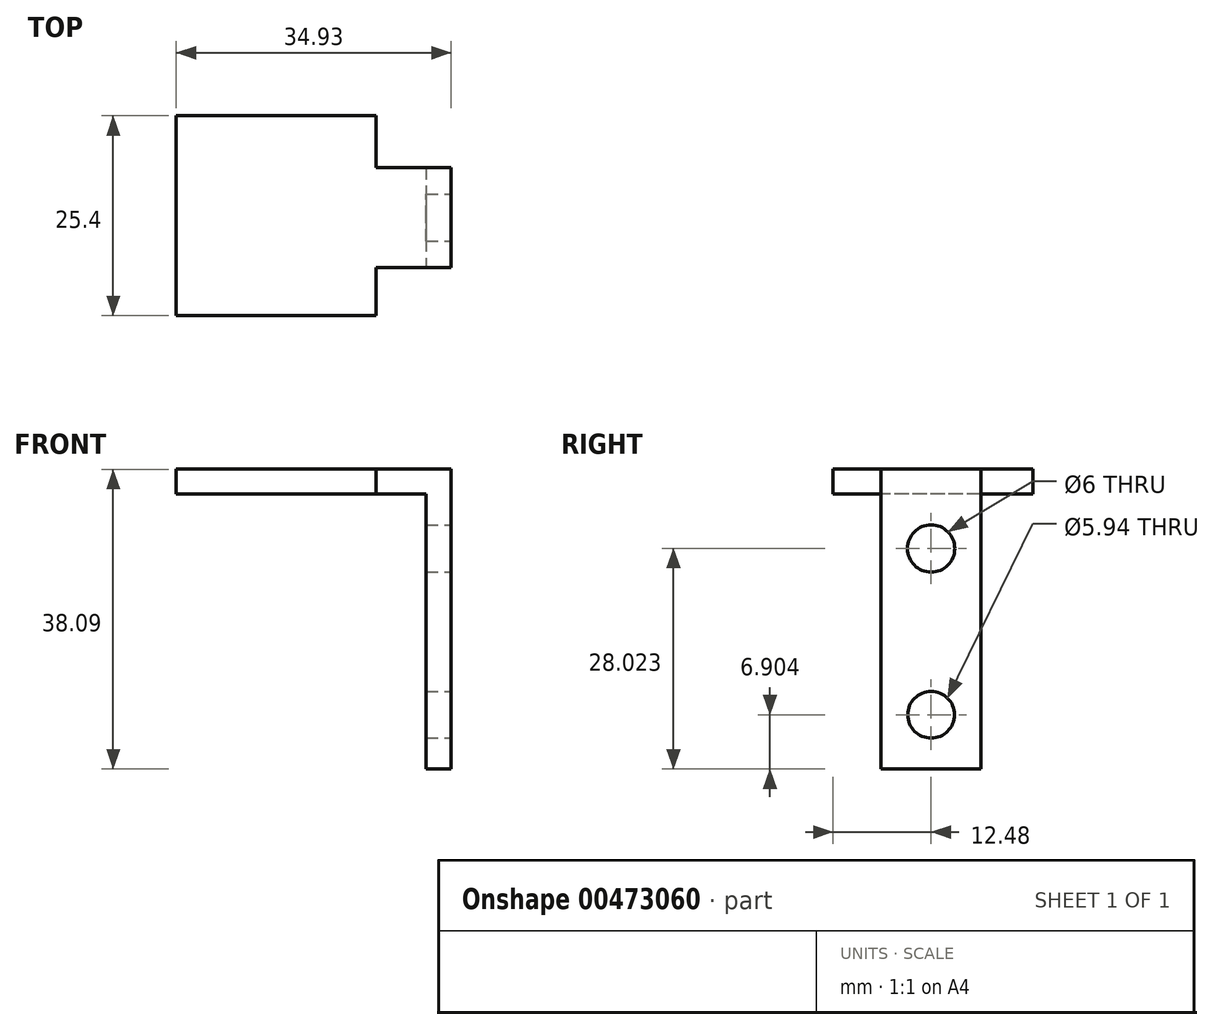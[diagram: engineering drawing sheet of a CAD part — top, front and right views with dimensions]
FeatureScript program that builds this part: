
annotation { "Feature Type Name" : "Feature", "Feature Type Description" : "" }
export const myFeature = defineFeature(function(context is Context, id is Id, definition is map)
    precondition{}
    {
        {
            var Q0;
            Q0=qCreatedBy(makeId("Top.planeOp"),FACE);
            var sketch = newSketch(context, id + "F0", { "sketchPlane" : qUnion([Q0])});
            skLineSegment(sketch, "E0.bottom", {"start": v(-11.79, 6.57) * mm, "end": v(13.61, 6.57) * mm});
            skLineSegment(sketch, "E0.top", {"start": v(-11.79, -18.83) * mm, "end": v(13.61, -18.83) * mm});
            skLineSegment(sketch, "E0.left", {"start": v(-11.79, 6.57) * mm, "end": v(-11.79, -18.83) * mm});
            skLineSegment(sketch, "E0.right", {"start": v(13.61, 6.57) * mm, "end": v(13.61, -18.83) * mm});
            skSolve(sketch);
        }
        {
            var Q0;
            Q0 = qSketchRegion(id + "F0", true);
            extrude(context, id + "F1", {"entities" : qUnion([Q0]), "depth" : 3.17 * mm});
        }
        {
            var Q0;
            Q0=makeQuery(id+"F1.opExtrude","SWEPT_FACE",FACE,{"disambiguationData":[OSD([sQuery(id+"F0.wireOp",EDGE,"E0.right")])]});
            var sketch = newSketch(context, id + "F2", { "sketchPlane" : qUnion([Q0])});
            skLineSegment(sketch, "E1.bottom", {"start": v(0, 3.18) * mm, "end": v(-12.7, 3.18) * mm});
            skLineSegment(sketch, "E1.top", {"start": v(0, 0) * mm, "end": v(-12.7, 0) * mm});
            skLineSegment(sketch, "E1.left", {"start": v(0, 3.18) * mm, "end": v(0, 0) * mm});
            skLineSegment(sketch, "E1.right", {"start": v(-12.7, 3.17) * mm, "end": v(-12.7, 0) * mm});
            skSolve(sketch);
        }
        {
            var Q0;
            Q0 = qSketchRegion(id + "F2", true);
            extrude(context, id + "F3", {"entities" : qUnion([Q0]), "operationType" : NewBodyOperationType.ADD, "depth" : 6.35 * mm});
        }
        {
            var Q0;
            Q0=makeQuery(id+"F3.opExtrude","CAP_FACE",FACE,{"disambiguationData":[OSD([sQuery(id+"F2.wireOp",EDGE,"E1.bottom"),sQuery(id+"F2.wireOp",EDGE,"E1.top"),sQuery(id+"F2.wireOp",EDGE,"E1.left"),sQuery(id+"F2.wireOp",EDGE,"E1.right")])],"isStart":false});
            var sketch = newSketch(context, id + "F4", { "sketchPlane" : qUnion([Q0])});
            skLineSegment(sketch, "E2.bottom", {"start": v(-12.7, 3.18) * mm, "end": v(0, 3.18) * mm});
            skLineSegment(sketch, "E2.top", {"start": v(-12.7, -34.93) * mm, "end": v(0, -34.93) * mm});
            skLineSegment(sketch, "E2.left", {"start": v(-12.7, 3.17) * mm, "end": v(-12.7, -34.93) * mm});
            skLineSegment(sketch, "E2.right", {"start": v(0, 3.17) * mm, "end": v(0, -34.93) * mm});
            skSolve(sketch);
        }
        {
            var Q0;
            Q0 = qSketchRegion(id + "F4", true);
            extrude(context, id + "F5", {"entities" : qUnion([Q0]), "operationType" : NewBodyOperationType.ADD, "depth" : 3.17 * mm});
        }
        {
            var Q0;
            Q0=makeQuery(id+"F5.opExtrude","CAP_FACE",FACE,{"disambiguationData":[OSD([sQuery(id+"F4.wireOp",EDGE,"E2.bottom"),sQuery(id+"F4.wireOp",EDGE,"E2.top"),sQuery(id+"F4.wireOp",EDGE,"E2.left"),sQuery(id+"F4.wireOp",EDGE,"E2.right")])],"isStart":false});
            var sketch = newSketch(context, id + "F6", { "sketchPlane" : qUnion([Q0])});
            skCircle(sketch, "E3", {"center": v(-6.35, -6.9) * mm, "radius": 3 * mm});
            skPoint(sketch, "E3.centerSnap0", {"position": v(-6.35, 3.18) * mm});
            skSolve(sketch);
        }
        {
            var Q0;
            Q0=makeQuery(id+"F6.imprint","IMPRINT",FACE,{"disambiguationData":[TD([[makeQuery(id+"F6.imprint","IMPRINT",EDGE,{"derivedFrom":sQuery(id+"F6.wireOp",EDGE,"E3")}),1.0]])]});
            extrude(context, id + "F7", {"entities" : qUnion([Q0]), "operationType" : NewBodyOperationType.REMOVE, "oppositeDirection" : true, "depth" : 3.2 * mm});
        }
        {
            var Q0;
            Q0=makeQuery(id+"F5.opExtrude","CAP_FACE",FACE,{"disambiguationData":[OSD([sQuery(id+"F4.wireOp",EDGE,"E2.bottom"),sQuery(id+"F4.wireOp",EDGE,"E2.top"),sQuery(id+"F4.wireOp",EDGE,"E2.left"),sQuery(id+"F4.wireOp",EDGE,"E2.right")])],"isStart":false});
            var sketch = newSketch(context, id + "F8", { "sketchPlane" : qUnion([Q0])});
            skCircle(sketch, "E4", {"center": v(-6.35, -28.02) * mm, "radius": 2.97 * mm});
            skPoint(sketch, "E4.centerSnap0", {"position": v(-6.35, 3.18) * mm});
            skSolve(sketch);
        }
        {
            var Q0;
            Q0=makeQuery(id+"F8.imprint","IMPRINT",FACE,{"disambiguationData":[TD([[makeQuery(id+"F8.imprint","IMPRINT",EDGE,{"derivedFrom":sQuery(id+"F8.wireOp",EDGE,"E4")}),1.0]])]});
            var sketch = newSketch(context, id + "F9", { "sketchPlane" : qUnion([Q0])});
            skSolve(sketch);
        }
        {
            var Q0;
            Q0=makeQuery(id+"F9.imprint","IMPRINT",FACE,{"disambiguationData":[TD([[makeQuery(id+"F9.imprint","IMPRINT",EDGE,{"derivedFrom":makeQuery(id+"F8.imprint","IMPRINT",EDGE,{"derivedFrom":sQuery(id+"F8.wireOp",EDGE,"E4")})}),1.0]])]});
            extrude(context, id + "F10", {"entities" : qUnion([Q0]), "operationType" : NewBodyOperationType.REMOVE, "oppositeDirection" : true, "depth" : 3.17 * mm});
        }
    });
